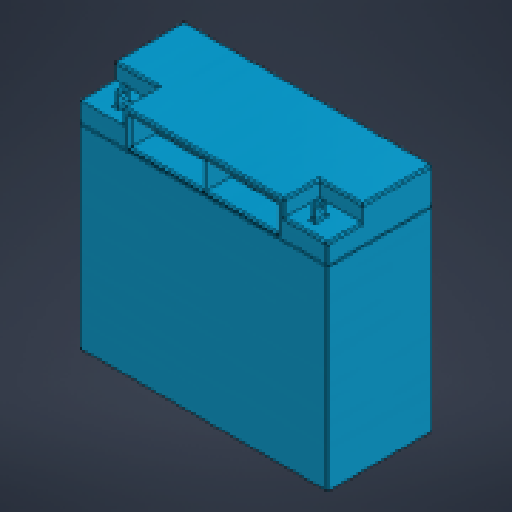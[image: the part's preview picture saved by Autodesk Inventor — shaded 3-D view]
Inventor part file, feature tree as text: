
AUTODESK INVENTOR PART (.ipt)
format: ipt  version: 2023 (Build 270158000, 158)  size: 266,752 bytes
history: mixed  units: in
note: dims shown in document units (in); Inventor stores cm internally (conversion verified against a paired STEP export)
features: fillet x1, imported_body x1
ambient origin geometry x8: Origin, YZ Plane, XZ Plane, XY Plane, X Axis, Y Axis, Z Axis, Center Point
bodies: Solid1 (imported_parasolid)
feature tree (2):
  fillet  "Fillet1"  [1 undecoded]
  imported_body  NMx_Import_Brep_tag  [imported B-rep: ~109 faces, bbox_mm=[180.34, 167.132, 76.2]]
note: 1 required parameter value undecoded (feature->parameter linkage not recoverable at this tier; creation-order binding heuristic only, values carry confidence <= 0.55)
